# Revit family: CSR4
name_source: partatom
category: Lighting Fixtures
revit_build: Autodesk Revit Architecture 2012 (Build: 20110309_2315(x64)
units: mm (PartAtom-declared; Revit-internal decimal feet)

## types (5) — shared parameters
Backbox = White
Color Filter = 16777215
Default Elevation = 48.000"
Description = 4' or 8' Industrial / 1, 2, or 3-Lamp T8 or T5
Dimming Lamp Color Temperature Shift = <None>
Emit from Line Length = 24.000"
Glass = Glass
Manufacturer = Columbia Lighting
Manufacturer Fax = 866.898.1065
Model = CSR4
Product Documentation Link = http://www.columbialighting.com
Product Page URL = http://www.columbialighting.com
Tilt Angle = -90.00°
URL = http://www.columbialighting.com

## per-type parameters (varying)
| type | Ballast Factor | Lamp | Photometric Web File | Wattage Comments |
| CSR4-132 | .88 | 1 | 10333.IES | 30W |
| CSR4-148 | .95 | 1 | 10200.IES | 67W |
| CSR4-232 | .88 | 2 | 10331.IES | 60W |
| CSR4-332 | .88 | 3 | 13410.IES | 88W |
| CSR4-332-U | .88 | 3 | 13410.IES | 88W |

## geometry (parser evidence)
native form markers: Sweep x1
no freeform markers — native parametric forms only
